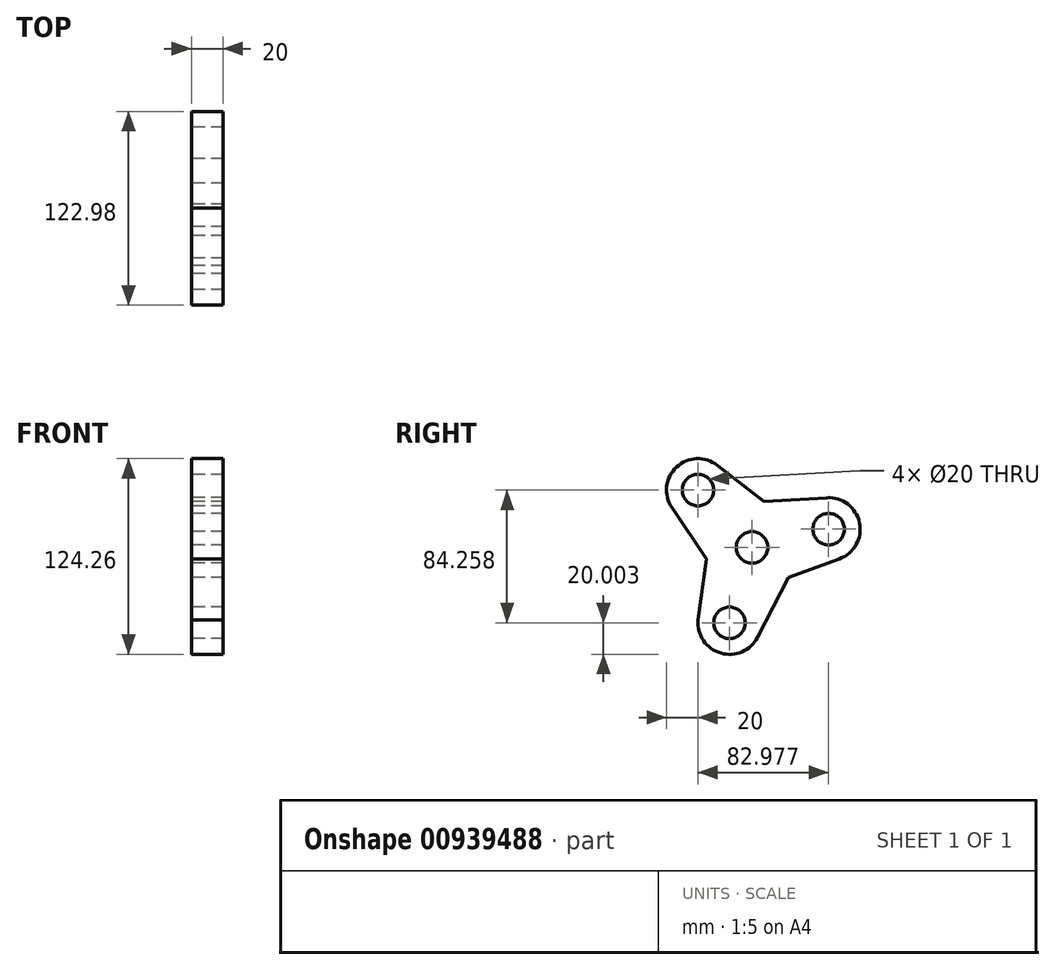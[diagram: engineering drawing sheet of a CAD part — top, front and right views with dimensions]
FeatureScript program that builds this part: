
annotation { "Feature Type Name" : "Feature", "Feature Type Description" : "" }
export const myFeature = defineFeature(function(context is Context, id is Id, definition is map)
    precondition{}
    {
        {
            var Q0;
            Q0=qCreatedBy(makeId("Right.planeOp"),FACE);
            var sketch = newSketch(context, id + "F0", { "sketchPlane" : qUnion([Q0])});
            skCircle(sketch, "E0", {"center": v(-34.33, 36.35) * mm, "radius": 10 * mm});
            skCircle(sketch, "E1", {"center": v(48.65, 11.55) * mm, "radius": 10 * mm});
            skCircle(sketch, "E2", {"center": v(-14.32, -47.9) * mm, "radius": 10 * mm});
            skCircle(sketch, "E3", {"center": v(0, 0) * mm, "radius": 10 * mm});
            skArc(sketch, "E4", {"start": v(-22.01, 52.1) * mm, "mid": v(-47.95, 51) * mm, "end": v(-50.94, 25.2) * mm});
            skArc(sketch, "E5", {"start": v(55.54, -7.22) * mm, "mid": v(68.22, 15.66) * mm, "end": v(47.41, 31.52) * mm});
            skArc(sketch, "E6", {"start": v(-34, -44.33) * mm, "mid": v(-20.77, -66.84) * mm, "end": v(3.44, -57.1) * mm});
            skCircle(sketch, "E7", {"center": v(0, 0) * mm, "radius": 30 * mm});
            skLineSegment(sketch, "E8", {"start": v(3.44, -57.1) * mm, "end": v(23.1, -19.14) * mm});
            skLineSegment(sketch, "E9", {"start": v(23.1, -19.14) * mm, "end": v(55.54, -7.22) * mm});
            skLineSegment(sketch, "E10", {"start": v(-34.24, -46.21) * mm, "end": v(-29.08, -7.37) * mm});
            skLineSegment(sketch, "E11", {"start": v(-29.08, -7.37) * mm, "end": v(-50.94, 25.2) * mm});
            skLineSegment(sketch, "E12", {"start": v(-22.01, 52.1) * mm, "end": v(7.48, 29.05) * mm});
            skLineSegment(sketch, "E13", {"start": v(7.48, 29.05) * mm, "end": v(47.41, 31.52) * mm});
            skSolve(sketch);
        }
        {
            var Q0;
            Q0=makeQuery(id+"F0.imprint","IMPRINT",FACE,{"disambiguationData":[TD([[makeQuery(id+"F0.imprint","IMPRINT",EDGE,{"derivedFrom":sQuery(id+"F0.wireOp",EDGE,"E0")}),-1.0]])]});
            var Q1;
            Q1=makeQuery(id+"F0.imprint","IMPRINT",FACE,{"disambiguationData":[TD([[makeQuery(id+"F0.imprint","IMPRINT",EDGE,{"derivedFrom":sQuery(id+"F0.wireOp",EDGE,"E1")}),-1.0]])]});
            var Q2;
            Q2=makeQuery(id+"F0.imprint","IMPRINT",FACE,{"disambiguationData":[TD([[makeQuery(id+"F0.imprint","IMPRINT",EDGE,{"derivedFrom":sQuery(id+"F0.wireOp",EDGE,"E2")}),-1.0]])]});
            var Q3;
            Q3=makeQuery(id+"F0.imprint","IMPRINT",FACE,{"disambiguationData":[TD([[makeQuery(id+"F0.imprint","IMPRINT",EDGE,{"derivedFrom":sQuery(id+"F0.wireOp",EDGE,"E3")}),-1.0]])]});
            extrude(context, id + "F1", {"entities" : qUnion([Q0, Q1, Q2, Q3]), "depth" : 20 * mm, "offsetDistance" : 25 * mm});
        }
    });
